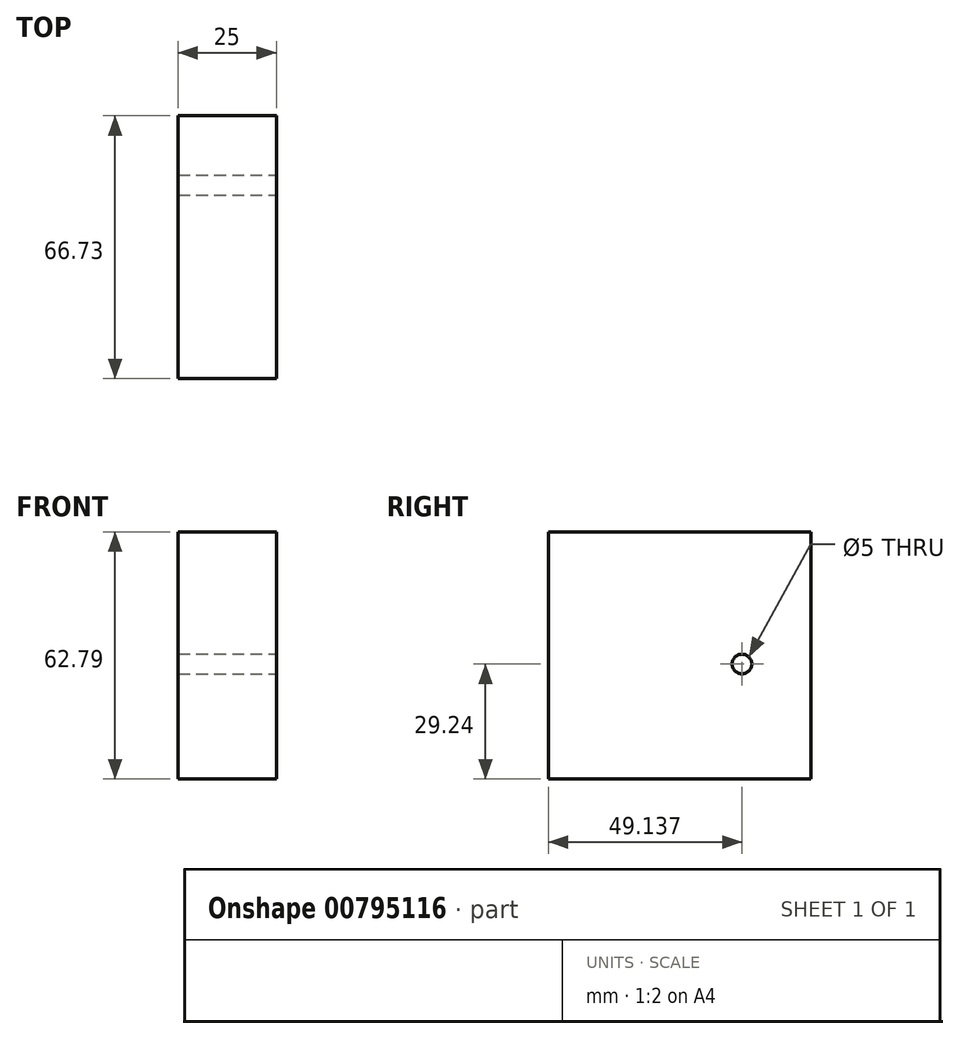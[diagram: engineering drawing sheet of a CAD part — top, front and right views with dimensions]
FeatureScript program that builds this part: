
annotation { "Feature Type Name" : "Feature", "Feature Type Description" : "" }
export const myFeature = defineFeature(function(context is Context, id is Id, definition is map)
    precondition{}
    {
        {
            var Q0;
            Q0=qCreatedBy(makeId("Right.planeOp"),FACE);
            var sketch = newSketch(context, id + "F0", { "sketchPlane" : qUnion([Q0])});
            skLineSegment(sketch, "E0.bottom", {"start": v(-56.95, 33.55) * mm, "end": v(9.78, 33.55) * mm});
            skLineSegment(sketch, "E0.top", {"start": v(-56.95, -29.24) * mm, "end": v(9.78, -29.24) * mm});
            skLineSegment(sketch, "E0.left", {"start": v(-56.95, 33.55) * mm, "end": v(-56.95, -29.24) * mm});
            skLineSegment(sketch, "E0.right", {"start": v(9.78, 33.55) * mm, "end": v(9.78, -29.24) * mm});
            skSolve(sketch);
        }
        {
            var Q0;
            Q0=makeQuery(id+"F0.imprint","IMPRINT",FACE,{"disambiguationData":[TD([[makeQuery(id+"F0.imprint","IMPRINT",EDGE,{"derivedFrom":sQuery(id+"F0.wireOp",EDGE,"E0.bottom")}),-1.0]])]});
            extrude(context, id + "F1", {"entities" : qUnion([Q0]), "depth" : 25 * mm, "offsetDistance" : 25 * mm});
        }
        {
            var Q0;
            Q0=makeQuery(id+"F1.opExtrude","CAP_FACE",FACE,{"disambiguationData":[OSD([sQuery(id+"F0.wireOp",EDGE,"E0.bottom"),sQuery(id+"F0.wireOp",EDGE,"E0.top"),sQuery(id+"F0.wireOp",EDGE,"E0.left"),sQuery(id+"F0.wireOp",EDGE,"E0.right")])],"isStart":false});
            var sketch = newSketch(context, id + "F2", { "sketchPlane" : qUnion([Q0])});
            skCircle(sketch, "E1", {"center": v(-27.52, 9.58) * mm, "radius": 10.82 * mm});
            skSolve(sketch);
        }
        {
            var Q0;
            Q0=makeQuery(id+"F2.imprint","IMPRINT",FACE,{"disambiguationData":[TD([[makeQuery(id+"F2.imprint","IMPRINT",EDGE,{"derivedFrom":sQuery(id+"F2.wireOp",EDGE,"E1")}),-1.0]])]});
            var sketch = newSketch(context, id + "F3", { "sketchPlane" : qUnion([Q0])});
            skCircle(sketch, "E2", {"center": v(-7.81, 0) * mm, "radius": 11.01 * mm});
            skCircle(sketch, "E3", {"center": v(-16.07, -7.29) * mm, "radius": 9.82 * mm});
            skSolve(sketch);
        }
        {
            var Q0;
            Q0=makeQuery(id+"F2.imprint","IMPRINT",FACE,{"disambiguationData":[TD([[makeQuery(id+"F2.imprint","IMPRINT",EDGE,{"derivedFrom":sQuery(id+"F2.wireOp",EDGE,"E1")}),1.0]])]});
            extrude(context, id + "F4", {"entities" : qUnion([Q0]), "operationType" : NewBodyOperationType.ADD, "depth" : -25 * mm, "offsetDistance" : 25 * mm});
        }
        {
            var Q0;
            Q0=sQuery(id+"F3.wireOp",VERTEX,"E2.center");
            var Q1;
            Q1=makeQuery(id+"F1.opExtrude","SWEPT_BODY",BODY,{"disambiguationData":[OSD([sQuery(id+"F0.wireOp",EDGE,"E0.bottom"),sQuery(id+"F0.wireOp",EDGE,"E0.top"),sQuery(id+"F0.wireOp",EDGE,"E0.left"),sQuery(id+"F0.wireOp",EDGE,"E0.right")])]});
            hole(context, id + "F5", {"style" : HoleStyle.SIMPLE, "endStyle" : HoleEndStyle.THROUGH, "holeDiameter" : 5 * mm, "majorDiameter" : 5 * mm, "isTappedThrough" : true, "tappedDepth" : 12 * mm, "tapClearance" : 3, "locations" : qUnion([Q0]), "scope" : qUnion([Q1])});
        }
    });
